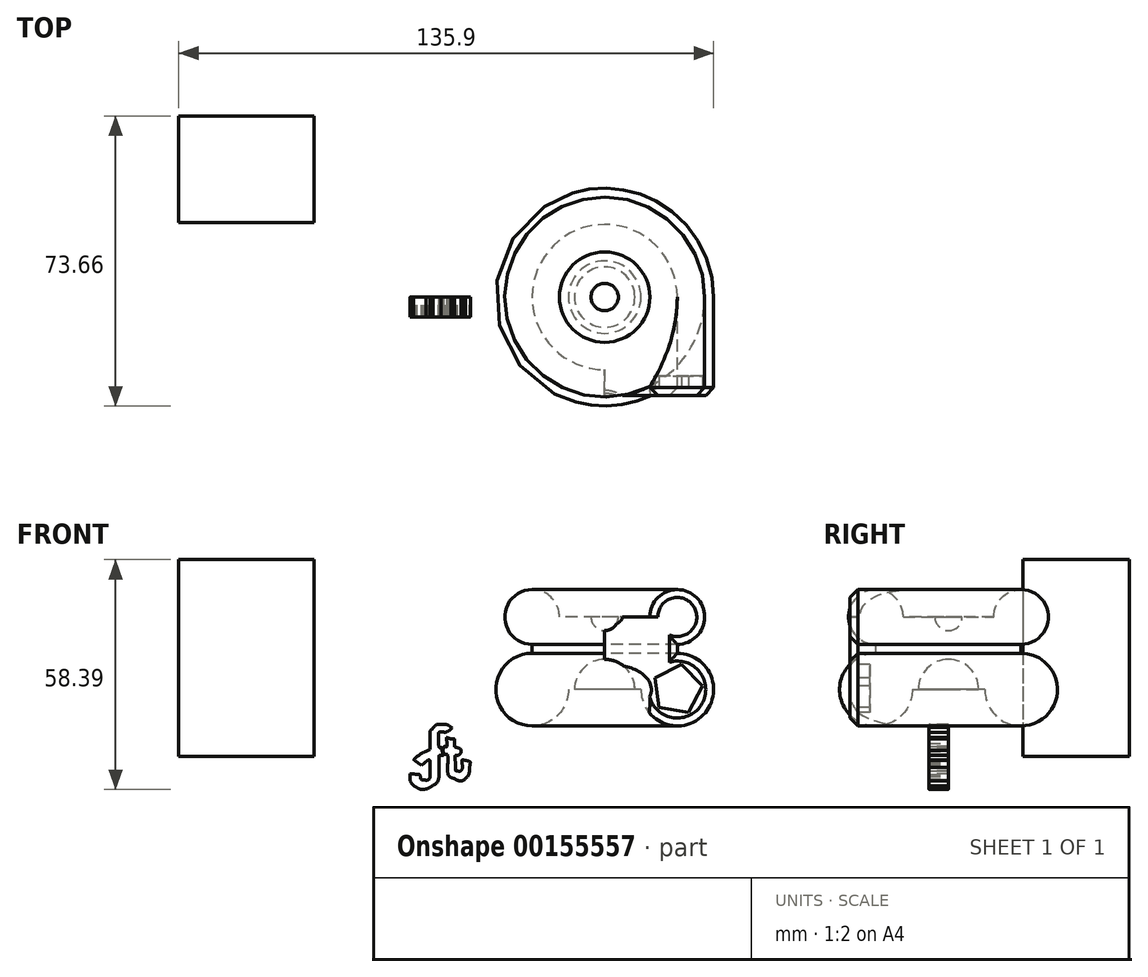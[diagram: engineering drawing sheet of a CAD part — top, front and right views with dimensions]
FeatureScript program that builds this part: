
annotation { "Feature Type Name" : "Feature", "Feature Type Description" : "" }
export const myFeature = defineFeature(function(context is Context, id is Id, definition is map)
    precondition{}
    {
        {
            var Q0;
            Q0=qCreatedBy(makeId("Front.planeOp"),FACE);
            var sketch = newSketch(context, id + "F0", { "sketchPlane" : qUnion([Q0])});
            skFitSpline(sketch, "E0", {"points": [v(-5.85, -7.87) * mm, v(-6.72, -7.37) * mm, v(-7.6, -6) * mm, v(-7.6, -5.13) * mm]});
            skFitSpline(sketch, "E1", {"points": [v(-7.6, -5.13) * mm, v(-7.6, -4.47) * mm, v(-7.52, -4.43) * mm, v(-6.35, -4.53) * mm]});
            skFitSpline(sketch, "E2", {"points": [v(-6.35, -4.53) * mm, v(-5.3, -4.6) * mm, v(-5.07, -4.74) * mm, v(-4.93, -5.3) * mm]});
            skFitSpline(sketch, "E3", {"points": [v(-4.93, -5.3) * mm, v(-4.81, -5.78) * mm, v(-4.56, -5.98) * mm, v(-4.1, -5.98) * mm]});
            skFitSpline(sketch, "E4", {"points": [v(-4.1, -5.98) * mm, v(-2.94, -5.98) * mm, v(-2.51, -5.16) * mm, v(-2.51, -2.93) * mm]});
            skFitSpline(sketch, "E5", {"points": [v(-2.51, -2.93) * mm, v(-2.51, -1.81) * mm, v(-2.63, -0.9) * mm, v(-2.78, -0.9) * mm]});
            skFitSpline(sketch, "E6", {"points": [v(-2.78, -0.9) * mm, v(-2.92, -0.9) * mm, v(-3.41, -1.22) * mm, v(-3.87, -1.6) * mm]});
            skFitSpline(sketch, "E7", {"points": [v(-5.51, -1.7) * mm, v(-5.96, -1.36) * mm, v(-6.37, -1.05) * mm, v(-6.42, -1.01) * mm]});
            skFitSpline(sketch, "E8", {"points": [v(-6.42, -1.01) * mm, v(-6.64, -0.86) * mm, v(-4.56, 0.8) * mm, v(-3.57, 1.24) * mm]});
            skLineSegment(sketch, "E9", {"start": v(-3.87, -1.6) * mm, "end": v(-4.7, -2.3) * mm});
            skLineSegment(sketch, "E10", {"start": v(-4.7, -2.3) * mm, "end": v(-5.51, -1.7) * mm});
            skFitSpline(sketch, "E11", {"points": [v(-2.51, 4.05) * mm, v(-2.51, 6.23) * mm, v(-2.46, 6.43) * mm, v(-1.7, 7.25) * mm]});
            skFitSpline(sketch, "E12", {"points": [v(-1.7, 7.25) * mm, v(-1.03, 7.96) * mm, v(-0.65, 8.13) * mm, v(0.3, 8.13) * mm]});
            skFitSpline(sketch, "E13", {"points": [v(0.3, 8.13) * mm, v(1.28, 8.13) * mm, v(2.32, 7.83) * mm, v(2.82, 7.4) * mm]});
            skFitSpline(sketch, "E14", {"points": [v(2.82, 7.4) * mm, v(3.05, 7.2) * mm, v(1.55, 6.17) * mm, v(1.01, 6.16) * mm]});
            skFitSpline(sketch, "E15", {"points": [v(1.01, 6.16) * mm, v(-0.17, 6.13) * mm, v(-0.4, 5.62) * mm, v(-0.3, 3.26) * mm]});
            skFitSpline(sketch, "E16", {"points": [v(-0.3, 3.26) * mm, v(-0.27, 2.53) * mm, v(-0.13, 2.2) * mm, v(0.17, 2.2) * mm]});
            skFitSpline(sketch, "E17", {"points": [v(0.17, 2.2) * mm, v(0.4, 2.2) * mm, v(0.59, 1.96) * mm, v(0.59, 1.66) * mm]});
            skFitSpline(sketch, "E18", {"points": [v(0.59, 1.66) * mm, v(0.59, 1.36) * mm, v(0.67, 0.92) * mm, v(0.76, 0.67) * mm]});
            skFitSpline(sketch, "E19", {"points": [v(0.76, 0.67) * mm, v(0.88, 0.35) * mm, v(0.76, 0.23) * mm, v(0.34, 0.23) * mm]});
            skFitSpline(sketch, "E20", {"points": [v(0.34, 0.23) * mm, v(-0.22, 0.23) * mm, v(-0.26, 0.08) * mm, v(-0.26, -2.33) * mm]});
            skFitSpline(sketch, "E21", {"points": [v(-0.26, -2.33) * mm, v(-0.26, -5.13) * mm, v(-0.8, -6.72) * mm, v(-2.04, -7.53) * mm]});
            skFitSpline(sketch, "E22", {"points": [v(-2.04, -7.53) * mm, v(-2.98, -8.14) * mm, v(-5.06, -8.33) * mm, v(-5.85, -7.87) * mm]});
            skLineSegment(sketch, "E23", {"start": v(-3.57, 1.24) * mm, "end": v(-2.51, 1.72) * mm});
            skLineSegment(sketch, "E24", {"start": v(-2.51, 1.72) * mm, "end": v(-2.51, 4.05) * mm});
            skFitSpline(sketch, "E25", {"points": [v(3.8, -5.68) * mm, v(2.5, -5.2) * mm, v(2, -4.1) * mm, v(2, -1.71) * mm]});
            skFitSpline(sketch, "E26", {"points": [v(2, -1.71) * mm, v(2, 0) * mm, v(1.91, 0.5) * mm, v(1.6, 0.5) * mm]});
            skFitSpline(sketch, "E27", {"points": [v(1.6, 0.5) * mm, v(1.18, 0.5) * mm, v(0.87, 1.1) * mm, v(0.87, 1.94) * mm]});
            skFitSpline(sketch, "E28", {"points": [v(0.87, 1.94) * mm, v(0.87, 2.27) * mm, v(1.07, 2.48) * mm, v(1.37, 2.48) * mm]});
            skFitSpline(sketch, "E29", {"points": [v(1.37, 2.48) * mm, v(1.8, 2.48) * mm, v(1.86, 2.68) * mm, v(1.76, 3.66) * mm]});
            skFitSpline(sketch, "E30", {"points": [v(1.76, 3.66) * mm, v(1.67, 4.67) * mm, v(1.72, 4.8) * mm, v(2.13, 4.64) * mm]});
            skFitSpline(sketch, "E31", {"points": [v(2.13, 4.64) * mm, v(2.4, 4.54) * mm, v(2.86, 4.46) * mm, v(3.15, 4.46) * mm]});
            skFitSpline(sketch, "E32", {"points": [v(3.15, 4.46) * mm, v(3.59, 4.46) * mm, v(3.7, 4.26) * mm, v(3.7, 3.46) * mm]});
            skFitSpline(sketch, "E33", {"points": [v(3.7, 3.46) * mm, v(3.7, 2.6) * mm, v(3.81, 2.41) * mm, v(4.54, 2.16) * mm]});
            skFitSpline(sketch, "E34", {"points": [v(4.54, 2.16) * mm, v(5, 2) * mm, v(5.38, 1.72) * mm, v(5.38, 1.54) * mm]});
            skFitSpline(sketch, "E35", {"points": [v(5.38, 1.54) * mm, v(5.36, 1.03) * mm, v(4.66, 0.23) * mm, v(4.23, 0.23) * mm]});
            skFitSpline(sketch, "E36", {"points": [v(4.23, 0.23) * mm, v(3.92, 0.23) * mm, v(3.86, -0.2) * mm, v(3.93, -1.75) * mm]});
            skFitSpline(sketch, "E37", {"points": [v(3.93, -1.75) * mm, v(4, -3.4) * mm, v(4.1, -3.73) * mm, v(4.5, -3.73) * mm]});
            skFitSpline(sketch, "E38", {"points": [v(4.5, -3.73) * mm, v(5.28, -3.73) * mm, v(5.67, -3.13) * mm, v(5.67, -1.94) * mm]});
            skFitSpline(sketch, "E39", {"points": [v(5.67, -1.94) * mm, v(5.67, -0.88) * mm, v(5.7, -0.85) * mm, v(6.45, -1.03) * mm]});
            skFitSpline(sketch, "E40", {"points": [v(6.45, -1.03) * mm, v(7.58, -1.31) * mm, v(7.73, -1.57) * mm, v(7.5, -2.87) * mm]});
            skFitSpline(sketch, "E41", {"points": [v(7.5, -2.87) * mm, v(7.17, -4.86) * mm, v(5.33, -6.25) * mm, v(3.8, -5.69) * mm]});
            skLineSegment(sketch, "E42", {"start": v(-5.85, -7.87) * mm, "end": v(-5.85, -7.87) * mm});
            skLineSegment(sketch, "E43", {"start": v(3.8, -5.69) * mm, "end": v(3.8, -5.68) * mm});
            skLineSegment(sketch, "E44", {"start": v(3.8, -5.68) * mm, "end": v(3.8, -5.69) * mm});
            skSolve(sketch);
        }
        {
            var Q0;
            Q0=makeQuery(id+"F0.imprint","IMPRINT",FACE,{"disambiguationData":[TD([[makeQuery(id+"F0.imprint","IMPRINT",EDGE,{"derivedFrom":sQuery(id+"F0.wireOp",EDGE,"E0")}),-1.0]])]});
            var Q1;
            Q1=makeQuery(id+"F0.imprint","IMPRINT",FACE,{"disambiguationData":[TD([[makeQuery(id+"F0.imprint","IMPRINT",EDGE,{"derivedFrom":sQuery(id+"F0.wireOp",EDGE,"E25")}),-1.0]])]});
            extrude(context, id + "F1", {"entities" : qUnion([Q0, Q1]), "depth" : 5 * mm});
        }
        {
            var Q0;
            Q0=qCreatedBy(makeId("Front.planeOp"),FACE);
            var sketch = newSketch(context, id + "F2", { "sketchPlane" : qUnion([Q0])});
            skLineSegment(sketch, "E45.bottom", {"start": v(60.3, 35.4) * mm, "end": v(41.86, 35.4) * mm});
            skLineSegment(sketch, "E45.top", {"start": v(60.3, 16.97) * mm, "end": v(41.86, 16.97) * mm});
            skLineSegment(sketch, "E45.left", {"start": v(60.3, 35.4) * mm, "end": v(60.3, 16.97) * mm});
            skLineSegment(sketch, "E45.right", {"start": v(41.86, 35.4) * mm, "end": v(41.86, 16.97) * mm});
            skCircle(sketch, "E46", {"center": v(60.3, 35.4) * mm, "radius": 6.96 * mm});
            skCircle(sketch, "E47", {"center": v(41.86, 35.4) * mm, "radius": 3.47 * mm});
            skCircle(sketch, "E48", {"center": v(41.86, 16.97) * mm, "radius": 7.67 * mm});
            skCircle(sketch, "E49", {"center": v(60.3, 16.97) * mm, "radius": 9.23 * mm});
            skSolve(sketch);
        }
        {
            var Q0;
            {var subQ0=sQuery(id+"F2.wireOp",EDGE,"E45.left");var subQ1=sQuery(id+"F2.wireOp",EDGE,"E45.bottom");var subQ2=makeQuery(id+"F2.imprint","INTERSECT",VERTEX,{"derivedFrom":[subQ1,subQ0]});Q0=makeQuery(id+"F2.imprint","IMPRINT",FACE,{"disambiguationData":[TD([[makeQuery(id+"F2.imprint","IMPRINT",EDGE,{"disambiguationData":[TD([[subQ2,-1.0]])],"derivedFrom":subQ1}),-1.0]])]});}
            var Q1;
            {var subQ0=sQuery(id+"F2.wireOp",EDGE,"E45.left");var subQ1=sQuery(id+"F2.wireOp",EDGE,"E45.top");var subQ2=makeQuery(id+"F2.imprint","INTERSECT",VERTEX,{"derivedFrom":[subQ1,subQ0]});Q1=makeQuery(id+"F2.imprint","IMPRINT",FACE,{"disambiguationData":[TD([[makeQuery(id+"F2.imprint","IMPRINT",EDGE,{"disambiguationData":[TD([[subQ2,-1.0]])],"derivedFrom":subQ1}),1.0]])]});}
            var Q2;
            {var subQ0=sQuery(id+"F2.wireOp",EDGE,"E46");var subQ13=sQuery(id+"F2.wireOp",EDGE,"E45.bottom");var subQ14=makeQuery(id+"F2.imprint","INTERSECT",VERTEX,{"derivedFrom":[subQ13,subQ0]});Q2=makeQuery(id+"F2.imprint","IMPRINT",FACE,{"disambiguationData":[TD([[makeQuery(id+"F2.imprint","IMPRINT",EDGE,{"disambiguationData":[TD([[subQ14,-1.0]])],"derivedFrom":subQ13}),1.0]])]});}
            var Q3;
            {var subQ0=sQuery(id+"F2.wireOp",EDGE,"E45.left");var subQ1=sQuery(id+"F2.wireOp",EDGE,"E45.top");var subQ2=makeQuery(id+"F2.imprint","INTERSECT",VERTEX,{"derivedFrom":[subQ1,subQ0]});Q3=makeQuery(id+"F2.imprint","IMPRINT",FACE,{"disambiguationData":[TD([[makeQuery(id+"F2.imprint","IMPRINT",EDGE,{"disambiguationData":[TD([[subQ2,-1.0]])],"derivedFrom":subQ1}),-1.0]])]});}
            var Q4;
            {var subQ0=sQuery(id+"F2.wireOp",EDGE,"E45.left");var subQ1=sQuery(id+"F2.wireOp",EDGE,"E45.bottom");var subQ2=makeQuery(id+"F2.imprint","INTERSECT",VERTEX,{"derivedFrom":[subQ1,subQ0]});Q4=makeQuery(id+"F2.imprint","IMPRINT",FACE,{"disambiguationData":[TD([[makeQuery(id+"F2.imprint","IMPRINT",EDGE,{"disambiguationData":[TD([[subQ2,-1.0]])],"derivedFrom":subQ1}),1.0]])]});}
            extrude(context, id + "F3", {"entities" : qUnion([Q0, Q1, Q2, Q3, Q4]), "depth" : 25 * mm});
        }
        {
            var Q0;
            Q0=makeQuery(id+"F3.opExtrude","CAP_FACE",FACE,{"disambiguationData":[OSD([sQuery(id+"F2.wireOp",EDGE,"E45.bottom"),sQuery(id+"F2.wireOp",EDGE,"E45.top"),sQuery(id+"F2.wireOp",EDGE,"E45.left"),sQuery(id+"F2.wireOp",EDGE,"E45.right"),sQuery(id+"F2.wireOp",EDGE,"E46"),sQuery(id+"F2.wireOp",EDGE,"E47"),sQuery(id+"F2.wireOp",EDGE,"E48"),sQuery(id+"F2.wireOp",EDGE,"E49")])],"isStart":true});
            var Q1;
            Q1=makeQuery(id+"F3.opExtrude","CAP_EDGE",EDGE,{"disambiguationData":[OSD([sQuery(id+"F2.wireOp",EDGE,"E45.right")])],"isStart":true});
            revolve(context, id + "F4", {"operationType" : NewBodyOperationType.ADD, "entities" : qUnion([Q0]), "axis" : qUnion([Q1]), "revolveType" : RevolveType.FULL});
        }
        {
            var Q0;
            Q0=makeQuery(id+"F3.opExtrude","CAP_FACE",FACE,{"disambiguationData":[OSD([sQuery(id+"F2.wireOp",EDGE,"E45.bottom"),sQuery(id+"F2.wireOp",EDGE,"E45.top"),sQuery(id+"F2.wireOp",EDGE,"E45.left"),sQuery(id+"F2.wireOp",EDGE,"E45.right"),sQuery(id+"F2.wireOp",EDGE,"E46"),sQuery(id+"F2.wireOp",EDGE,"E47"),sQuery(id+"F2.wireOp",EDGE,"E48"),sQuery(id+"F2.wireOp",EDGE,"E49")])],"isStart":false});
            var sketch = newSketch(context, id + "F5", { "sketchPlane" : qUnion([Q0])});
            skCircle(sketch, "E50.cCircle", {"center": v(60.3, 16.97) * mm, "radius": 5.2 * mm, "construction": true});
            skLineSegment(sketch, "E50.0", {"start": v(54.6, 19.95) * mm, "end": v(61.38, 23.31) * mm});
            skLineSegment(sketch, "E50.1", {"start": v(61.38, 23.31) * mm, "end": v(66.67, 17.9) * mm});
            skLineSegment(sketch, "E50.2", {"start": v(66.67, 17.9) * mm, "end": v(63.17, 11.2) * mm});
            skLineSegment(sketch, "E50.3", {"start": v(63.17, 11.2) * mm, "end": v(55.7, 12.46) * mm});
            skLineSegment(sketch, "E50.4", {"start": v(55.7, 12.46) * mm, "end": v(54.6, 19.95) * mm});
            skPoint(sketch, "E50.0.midPoint", {"position": v(58, 21.63) * mm});
            skSolve(sketch);
        }
        {
            var Q0;
            Q0=makeQuery(id+"F5.imprint","IMPRINT",FACE,{"disambiguationData":[TD([[makeQuery(id+"F5.imprint","IMPRINT",EDGE,{"derivedFrom":sQuery(id+"F5.wireOp",EDGE,"E50.0")}),-1.0]])]});
            extrude(context, id + "F6", {"entities" : qUnion([Q0]), "operationType" : NewBodyOperationType.REMOVE, "oppositeDirection" : true, "depth" : 5 * mm});
        }
        {
            var Q0;
            Q0=makeQuery(id+"F3.opExtrude","CAP_EDGE",EDGE,{"disambiguationData":[OSD([sQuery(id+"F2.wireOp",EDGE,"E49")])],"isStart":false});
            var Q1;
            Q1=makeQuery(id+"F3.opExtrude","CAP_EDGE",EDGE,{"disambiguationData":[OSD([sQuery(id+"F2.wireOp",EDGE,"E45.left")])],"isStart":false});
            var Q2;
            Q2=makeQuery(id+"F3.opExtrude","CAP_EDGE",EDGE,{"disambiguationData":[OSD([sQuery(id+"F2.wireOp",EDGE,"E46")])],"isStart":false});
            chamfer(context, id + "F7", {"entities" : qUnion([Q0, Q1, Q2]), "width" : 2 * mm, "tangentPropagation" : true});
        }
        {
            var Q0;
            Q0=qCreatedBy(makeId("Top.planeOp"),FACE);
            var sketch = newSketch(context, id + "F8", { "sketchPlane" : qUnion([Q0])});
            skLineSegment(sketch, "E51.bottom", {"start": v(-32, 45.98) * mm, "end": v(-66.36, 45.98) * mm});
            skLineSegment(sketch, "E51.top", {"start": v(-32, 18.92) * mm, "end": v(-66.36, 18.92) * mm});
            skLineSegment(sketch, "E51.left", {"start": v(-32, 45.98) * mm, "end": v(-32, 18.92) * mm});
            skLineSegment(sketch, "E51.right", {"start": v(-66.36, 45.98) * mm, "end": v(-66.36, 18.92) * mm});
            skSolve(sketch);
        }
        {
            var Q0;
            Q0=makeQuery(id+"F8.imprint","IMPRINT",FACE,{"disambiguationData":[TD([[makeQuery(id+"F8.imprint","IMPRINT",EDGE,{"derivedFrom":sQuery(id+"F8.wireOp",EDGE,"E51.bottom")}),1.0]])]});
            extrude(context, id + "F9", {"entities" : qUnion([Q0]), "depth" : 50 * mm});
        }
    });
